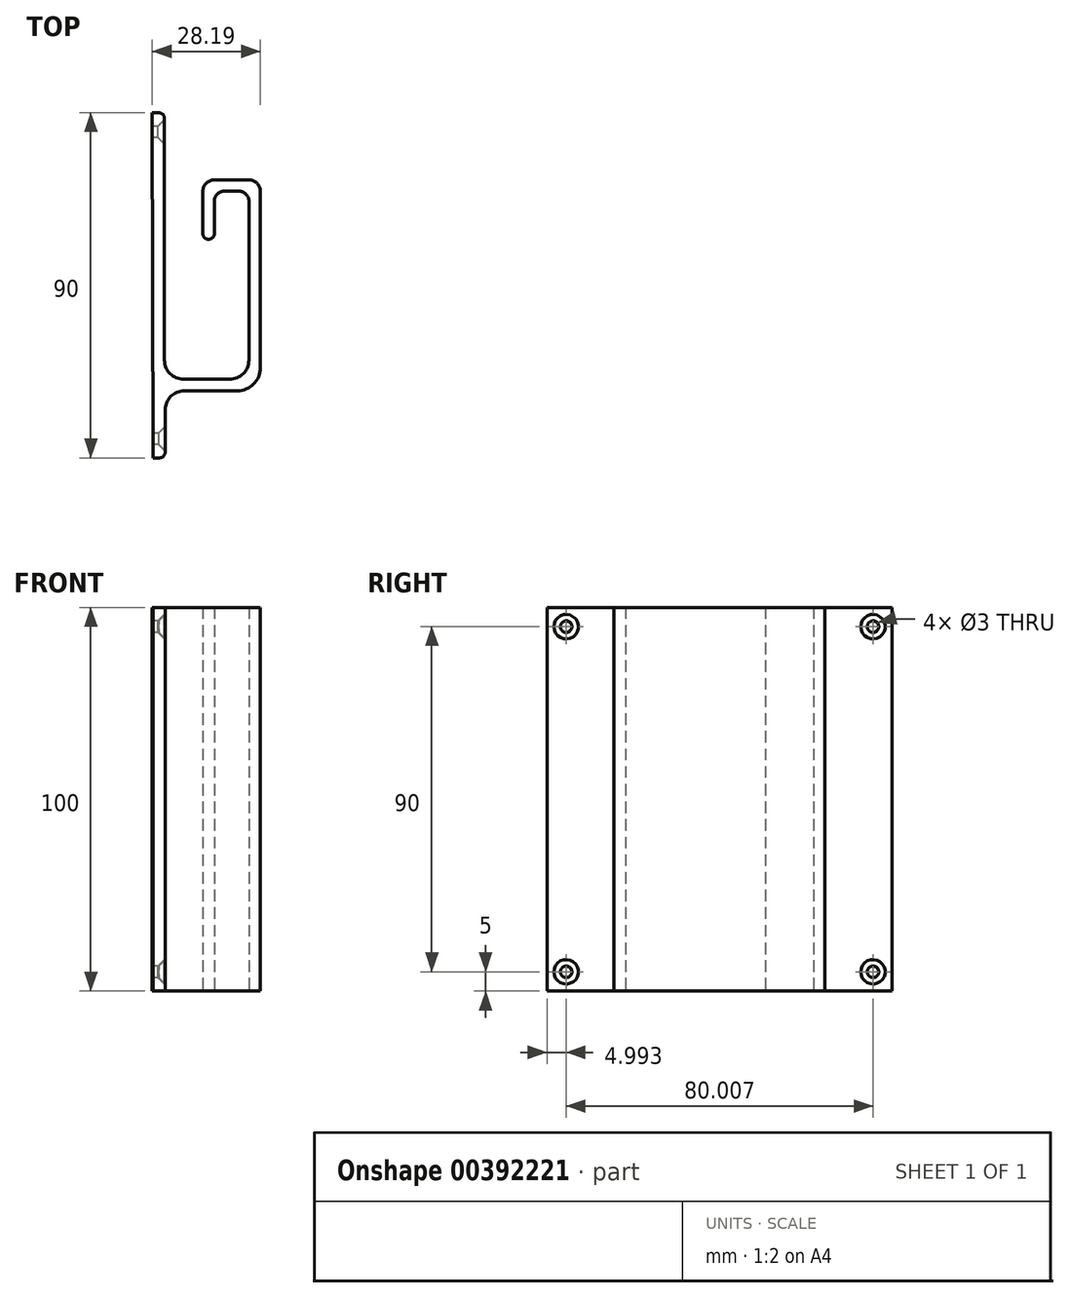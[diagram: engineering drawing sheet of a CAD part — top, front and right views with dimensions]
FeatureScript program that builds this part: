
annotation { "Feature Type Name" : "Feature", "Feature Type Description" : "" }
export const myFeature = defineFeature(function(context is Context, id is Id, definition is map)
    precondition{}
    {
        {
            var Q0;
            Q0=qCreatedBy(makeId("Top.planeOp"),FACE);
            var sketch = newSketch(context, id + "F0", { "sketchPlane" : qUnion([Q0])});
            skLineSegment(sketch, "E0.bottom", {"start": v(0.19, -45) * mm, "end": v(-1.5, -45) * mm});
            skLineSegment(sketch, "E0.top", {"start": v(0, 45) * mm, "end": v(-1.69, 45) * mm});
            skLineSegment(sketch, "E0.right", {"start": v(-1.5, -45) * mm, "end": v(-1.69, 45) * mm});
            skPoint(sketch, "E0.middle", {"position": v(0, 0) * mm});
            skLineSegment(sketch, "E1.top", {"start": v(6.69, -27.5) * mm, "end": v(20.5, -27.5) * mm});
            skLineSegment(sketch, "E1.right", {"start": v(26.5, -14) * mm, "end": v(26.5, -21.5) * mm});
            skLineSegment(sketch, "E2.left", {"start": v(26.5, -14) * mm, "end": v(26.5, 24.5) * mm});
            skLineSegment(sketch, "E3.right", {"start": v(11.5, 24.5) * mm, "end": v(11.5, 17) * mm});
            skLineSegment(sketch, "E4.top", {"start": v(13, 12) * mm, "end": v(13, 12) * mm});
            skLineSegment(sketch, "E4.left", {"start": v(11.5, 17) * mm, "end": v(11.5, 13.5) * mm});
            skLineSegment(sketch, "E4.right", {"start": v(14.5, 22) * mm, "end": v(14.5, 13.5) * mm});
            skPoint(sketch, "E5.visualSharp", {"position": v(1.69, -45) * mm});
            skArc(sketch, "E5.filletArc", {"start": v(0.19, -45) * mm, "mid": v(1.25, -44.56) * mm, "end": v(1.69, -43.5) * mm});
            skPoint(sketch, "E6.visualSharp", {"position": v(26.5, -27.5) * mm});
            skArc(sketch, "E6.filletArc", {"start": v(20.5, -27.5) * mm, "mid": v(24.74, -25.74) * mm, "end": v(26.5, -21.5) * mm});
            skArc(sketch, "E7.filletArc", {"start": v(26.5, 24.5) * mm, "mid": v(25.62, 26.62) * mm, "end": v(23.5, 27.5) * mm});
            skArc(sketch, "E8.filletArc", {"start": v(14.5, 27.5) * mm, "mid": v(12.38, 26.62) * mm, "end": v(11.5, 24.5) * mm});
            skPoint(sketch, "E9.visualSharp", {"position": v(11.5, 12) * mm});
            skArc(sketch, "E9.filletArc", {"start": v(11.5, 13.5) * mm, "mid": v(11.94, 12.44) * mm, "end": v(13, 12) * mm});
            skPoint(sketch, "E10.visualSharp", {"position": v(14.5, 12) * mm});
            skArc(sketch, "E10.filletArc", {"start": v(13, 12) * mm, "mid": v(14.06, 12.44) * mm, "end": v(14.5, 13.5) * mm});
            skPoint(sketch, "E11.visualSharp", {"position": v(1.5, 45) * mm});
            skArc(sketch, "E11.filletArc", {"start": v(1.5, 43.5) * mm, "mid": v(1.06, 44.56) * mm, "end": v(0, 45) * mm});
            skLineSegment(sketch, "E12", {"start": v(17, 24.5) * mm, "end": v(21, 24.5) * mm});
            skArc(sketch, "E13.filletArc", {"start": v(17, 24.5) * mm, "mid": v(15.23, 23.77) * mm, "end": v(14.5, 22) * mm});
            skLineSegment(sketch, "E14", {"start": v(23.5, 22) * mm, "end": v(23.5, -19.5) * mm});
            skLineSegment(sketch, "E15", {"start": v(18.5, -24.5) * mm, "end": v(6.5, -24.5) * mm});
            skArc(sketch, "E16.filletArc", {"start": v(23.5, 22) * mm, "mid": v(22.77, 23.77) * mm, "end": v(21, 24.5) * mm});
            skPoint(sketch, "E17.visualSharp", {"position": v(23.5, -24.5) * mm});
            skArc(sketch, "E17.filletArc", {"start": v(18.5, -24.5) * mm, "mid": v(22.04, -23.04) * mm, "end": v(23.5, -19.5) * mm});
            skLineSegment(sketch, "E18", {"start": v(1.69, -43.5) * mm, "end": v(1.69, -32.5) * mm});
            skLineSegment(sketch, "E19", {"start": v(1.5, -19.5) * mm, "end": v(1.5, 43.5) * mm});
            skPoint(sketch, "E20.visualSharp", {"position": v(1.5, -24.5) * mm});
            skArc(sketch, "E20.filletArc", {"start": v(1.5, -19.5) * mm, "mid": v(2.96, -23.04) * mm, "end": v(6.5, -24.5) * mm});
            skPoint(sketch, "E21.visualSharp", {"position": v(1.69, -27.5) * mm});
            skArc(sketch, "E21.filletArc", {"start": v(6.69, -27.5) * mm, "mid": v(3.15, -28.96) * mm, "end": v(1.69, -32.5) * mm});
            skLineSegment(sketch, "E22", {"start": v(14.5, 27.5) * mm, "end": v(23.5, 27.5) * mm});
            skSolve(sketch);
        }
        {
            var Q0;
            Q0=makeQuery(id+"F0.imprint","IMPRINT",FACE,{"disambiguationData":[TD([[makeQuery(id+"F0.imprint","IMPRINT",EDGE,{"derivedFrom":sQuery(id+"F0.wireOp",EDGE,"E0.bottom")}),-1.0]])]});
            extrude(context, id + "F1", {"entities" : qUnion([Q0]), "depth" : 100 * mm});
        }
        {
            var Q0;
            Q0=makeQuery(id+"F1.opExtrude","SWEPT_FACE",FACE,{"disambiguationData":[OSD([sQuery(id+"F0.wireOp",EDGE,"E0.right")])]});
            var sketch = newSketch(context, id + "F2", { "sketchPlane" : qUnion([Q0])});
            skCircle(sketch, "E23", {"center": v(-40, 5) * mm, "radius": 1.5 * mm});
            skLineSegment(sketch, "E24", {"start": v(0, 0) * mm, "end": v(0, 100) * mm, "construction": true});
            skLineSegment(sketch, "E25", {"start": v(-45, 50) * mm, "end": v(45, 50) * mm, "construction": true});
            skCircle(sketch, "E26.MirrorC", {"center": v(-40, 95) * mm, "radius": 1.5 * mm});
            skCircle(sketch, "E27.MirrorC", {"center": v(40, 5) * mm, "radius": 1.5 * mm});
            skCircle(sketch, "E28.MirrorC", {"center": v(40, 95) * mm, "radius": 1.5 * mm});
            skSolve(sketch);
        }
        {
            var Q0;
            Q0=qSketchRegion(id+"F2",true);
            extrude(context, id + "F3", {"entities" : qUnion([Q0]), "operationType" : NewBodyOperationType.REMOVE, "endBound" : BoundingType.THROUGH_ALL, "oppositeDirection" : true, "depth" : 25 * mm});
        }
        {
            var Q0;
            Q0=makeQuery(id+"F3.boolean.opBoolean","INTERSECT",EDGE,{"derivedFrom":[makeQuery(id+"F1.opExtrude","SWEPT_FACE",FACE,{"disambiguationData":[OSD([sQuery(id+"F0.wireOp",EDGE,"E18")])]}),makeQuery(id+"F3.opExtrude","SWEPT_FACE",FACE,{"disambiguationData":[OSD([sQuery(id+"F2.wireOp",EDGE,"E28.MirrorC")])]})]});
            var Q1;
            Q1=makeQuery(id+"F3.boolean.opBoolean","INTERSECT",EDGE,{"derivedFrom":[makeQuery(id+"F1.opExtrude","SWEPT_FACE",FACE,{"disambiguationData":[OSD([sQuery(id+"F0.wireOp",EDGE,"E19")])]}),makeQuery(id+"F3.opExtrude","SWEPT_FACE",FACE,{"disambiguationData":[OSD([sQuery(id+"F2.wireOp",EDGE,"E26.MirrorC")])]})]});
            var Q2;
            Q2=makeQuery(id+"F3.boolean.opBoolean","INTERSECT",EDGE,{"derivedFrom":[makeQuery(id+"F1.opExtrude","SWEPT_FACE",FACE,{"disambiguationData":[OSD([sQuery(id+"F0.wireOp",EDGE,"E19")])]}),makeQuery(id+"F3.opExtrude","SWEPT_FACE",FACE,{"disambiguationData":[OSD([sQuery(id+"F2.wireOp",EDGE,"E23")])]})]});
            var Q3;
            Q3=makeQuery(id+"F3.boolean.opBoolean","INTERSECT",EDGE,{"derivedFrom":[makeQuery(id+"F1.opExtrude","SWEPT_FACE",FACE,{"disambiguationData":[OSD([sQuery(id+"F0.wireOp",EDGE,"E18")])]}),makeQuery(id+"F3.opExtrude","SWEPT_FACE",FACE,{"disambiguationData":[OSD([sQuery(id+"F2.wireOp",EDGE,"E27.MirrorC")])]})]});
            chamfer(context, id + "F4", {"entities" : qUnion([Q0, Q1, Q2, Q3]), "width" : 1.7 * mm, "tangentPropagation" : true});
        }
    });
